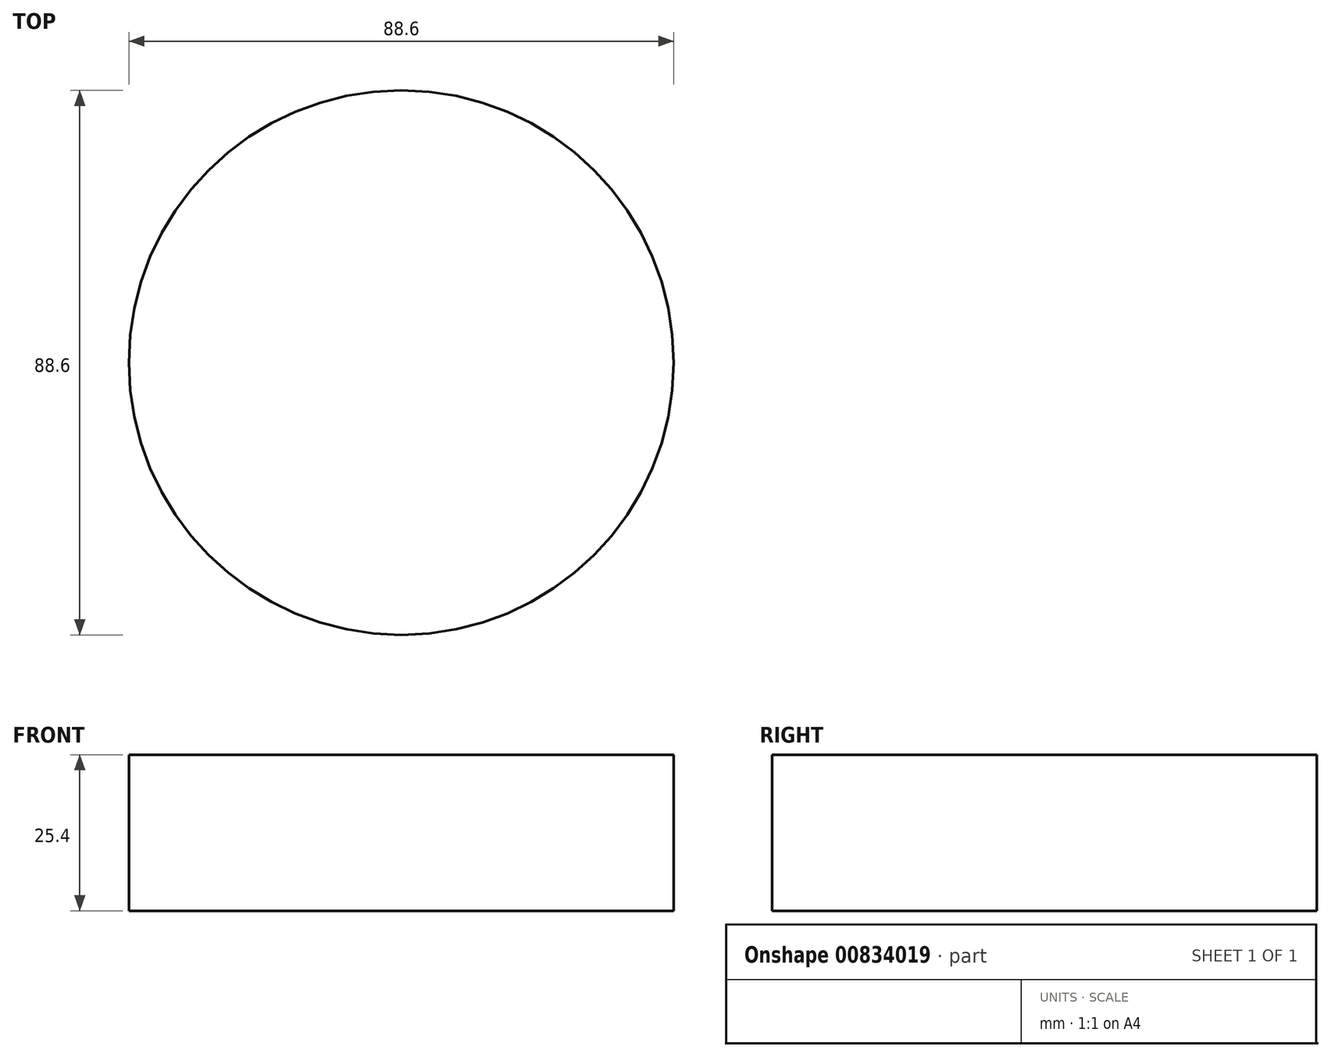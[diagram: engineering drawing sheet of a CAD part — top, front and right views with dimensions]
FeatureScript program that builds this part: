
annotation { "Feature Type Name" : "Feature", "Feature Type Description" : "" }
export const myFeature = defineFeature(function(context is Context, id is Id, definition is map)
    precondition{}
    {
        {
            var Q0;
            Q0=qCreatedBy(makeId("Top.planeOp"),FACE);
            var sketch = newSketch(context, id + "F0", { "sketchPlane" : qUnion([Q0])});
            skCircle(sketch, "E0", {"center": v(0, 41.14) * mm, "radius": 43.8 * mm});
            skCircle(sketch, "E1", {"center": v(0, 0) * mm, "radius": 44.3 * mm});
            skSolve(sketch);
        }
        {
            var Q0;
            Q0=sQuery(id+"F0.wireOp",EDGE,"E1");
            extrude(context, id + "F1", {"bodyType" : ToolBodyType.SURFACE, "surfaceEntities" : qUnion([Q0]), "depth" : 25.4 * mm, "offsetDistance" : 25.4 * mm});
        }
    });
